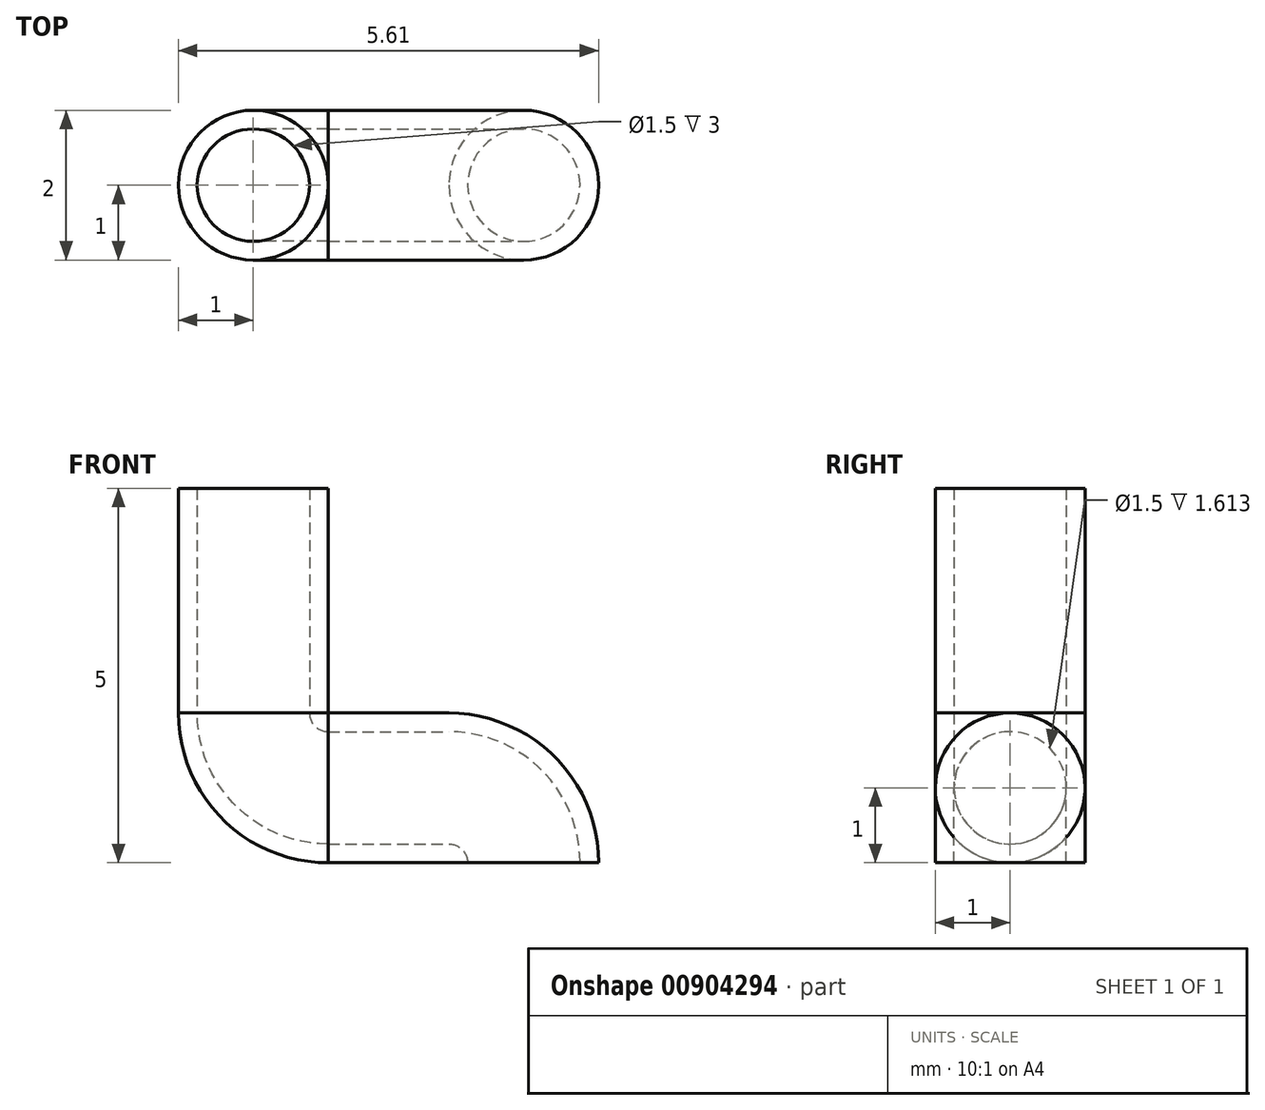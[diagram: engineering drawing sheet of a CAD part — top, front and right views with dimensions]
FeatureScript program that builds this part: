
annotation { "Feature Type Name" : "Feature", "Feature Type Description" : "" }
export const myFeature = defineFeature(function(context is Context, id is Id, definition is map)
    precondition{}
    {
        {
            var Q0;
            Q0=qCreatedBy(makeId("Top.planeOp"),FACE);
            var sketch = newSketch(context, id + "F0", { "sketchPlane" : qUnion([Q0])});
            skLineSegment(sketch, "E0.bottom", {"start": v(3.61, 0) * mm, "end": v(-3.61, 0) * mm});
            skLineSegment(sketch, "E0.top", {"start": v(3.61, 0) * mm, "end": v(-3.61, 0) * mm});
            skLineSegment(sketch, "E0.left", {"start": v(3.61, 0) * mm, "end": v(3.61, 0) * mm});
            skLineSegment(sketch, "E0.right", {"start": v(-3.61, 0) * mm, "end": v(-3.61, 0) * mm});
            skPoint(sketch, "E0.middle", {"position": v(0, 0) * mm});
            skCircle(sketch, "E1", {"center": v(-3.61, 0) * mm, "radius": 0.75 * mm});
            skCircle(sketch, "E2", {"center": v(-3.61, 0) * mm, "radius": 1 * mm});
            skCircle(sketch, "E3", {"center": v(3.61, 0) * mm, "radius": 0.75 * mm});
            skCircle(sketch, "E4", {"center": v(3.61, 0) * mm, "radius": 1 * mm});
            skSolve(sketch);
        }
        {
            var Q0;
            Q0=qCreatedBy(makeId("Front.planeOp"),FACE);
            var sketch = newSketch(context, id + "F1", { "sketchPlane" : qUnion([Q0])});
            skLineSegment(sketch, "E5.0", {"start": v(-4.61, 0) * mm, "end": v(-2.61, 0) * mm});
            skLineSegment(sketch, "E6.0", {"start": v(2.61, 0) * mm, "end": v(4.61, 0) * mm});
            skLineSegment(sketch, "E7", {"start": v(-2.61, 0) * mm, "end": v(-2.61, 2) * mm});
            skLineSegment(sketch, "E8", {"start": v(-2.61, 1) * mm, "end": v(-1.94, 1) * mm});
            skArc(sketch, "E9", {"start": v(-2.61, 1) * mm, "mid": v(-3.32, 0.7) * mm, "end": v(-3.61, 0) * mm});
            skLineSegment(sketch, "E10", {"start": v(0, 0) * mm, "end": v(0, 0.78) * mm});
            skLineSegment(sketch, "E11.MirrorCS", {"start": v(2.61, 0) * mm, "end": v(2.61, 2) * mm});
            skArc(sketch, "E12.MirrorCS", {"start": v(2.61, 1) * mm, "mid": v(3.32, 0.7) * mm, "end": v(3.61, 0) * mm});
            skSolve(sketch);
        }
        {
            var Q0;
            Q0=makeQuery(id+"F0.imprint","IMPRINT",FACE,{"disambiguationData":[TD([[makeQuery(id+"F0.imprint","IMPRINT",EDGE,{"derivedFrom":sQuery(id+"F0.wireOp",EDGE,"E1")}),-1.0]])]});
            var Q1;
            Q1=sQuery(id+"F1.wireOp",EDGE,"E9");
            sweep(context, id + "F2", {"profiles" : qUnion([Q0]), "path" : qUnion([Q1])});
        }
        {
            var Q0;
            Q0=makeQuery(id+"F0.imprint","IMPRINT",FACE,{"disambiguationData":[TD([[makeQuery(id+"F0.imprint","IMPRINT",EDGE,{"derivedFrom":sQuery(id+"F0.wireOp",EDGE,"E3")}),-1.0]])]});
            var Q1;
            Q1=sQuery(id+"F1.wireOp",EDGE,"E12.MirrorCS");
            sweep(context, id + "F3", {"profiles" : qUnion([Q0]), "path" : qUnion([Q1])});
        }
        {
            var Q0;
            Q0=makeQuery(id+"F3.opSweep","CAP_FACE",FACE,{"disambiguationData":[OSD([sQuery(id+"F0.wireOp",EDGE,"E3"),sQuery(id+"F0.wireOp",EDGE,"E4"),sQuery(id+"F1.wireOp",VERTEX,"E12.MirrorCS.start")])],"isStart":false});
            extrude(context, id + "F4", {"entities" : qUnion([Q0]), "operationType" : NewBodyOperationType.ADD, "depth" : 2.6 * mm, "offsetDistance" : 25 * mm});
        }
        {
            var Q0;
            Q0=makeQuery(id+"F2.opSweep","CAP_FACE",FACE,{"disambiguationData":[OSD([sQuery(id+"F0.wireOp",EDGE,"E1"),sQuery(id+"F0.wireOp",EDGE,"E2"),sQuery(id+"F1.wireOp",VERTEX,"E9.start")])],"isStart":false});
            extrude(context, id + "F5", {"entities" : qUnion([Q0]), "depth" : 2.6 * mm, "offsetDistance" : 25 * mm});
        }
        {
            var Q0;
            Q0=makeQuery(id+"F2.opSweep","SWEPT_BODY",BODY,{"disambiguationData":[OSD([sQuery(id+"F0.wireOp",EDGE,"E1"),sQuery(id+"F0.wireOp",EDGE,"E2"),sQuery(id+"F1.wireOp",EDGE,"E9")])]});
            var Q1;
            Q1=makeQuery(id+"F3.opSweep","SWEPT_BODY",BODY,{"disambiguationData":[OSD([sQuery(id+"F0.wireOp",EDGE,"E3"),sQuery(id+"F0.wireOp",EDGE,"E4"),sQuery(id+"F1.wireOp",EDGE,"E12.MirrorCS")])]});
            var Q2;
            Q2=makeQuery(id+"F5.opExtrude","SWEPT_BODY",BODY,{"disambiguationData":[OSD([sQuery(id+"F0.wireOp",EDGE,"E1"),sQuery(id+"F0.wireOp",EDGE,"E2"),sQuery(id+"F1.wireOp",VERTEX,"E9.start")])]});
            booleanBodies(context, id + "F6", {"operationType" : BooleanOperationType.UNION, "tools" : qUnion([Q0, Q1, Q2])});
        }
        {
            var Q0;
            Q0=qCreatedBy(makeId("Top.planeOp"),FACE);
            cPlane(context, id + "F7", {"entities" : qUnion([Q0]), "cplaneType" : CPlaneType.OFFSET, "offset" : 1 * mm, "width" : 150 * mm, "height" : 150 * mm});
        }
        {
            var Q0;
            Q0=qCreatedBy(id+"F7.planeOp",FACE);
            var sketch = newSketch(context, id + "F8", { "sketchPlane" : qUnion([Q0])});
            skCircle(sketch, "E13", {"center": v(0, 0) * mm, "radius": 1 * mm});
            skCircle(sketch, "E14", {"center": v(0, 0) * mm, "radius": 0.75 * mm});
            skSolve(sketch);
        }
        {
            var Q0;
            Q0=makeQuery(id+"F8.imprint","IMPRINT",FACE,{"disambiguationData":[TD([[makeQuery(id+"F8.imprint","IMPRINT",EDGE,{"derivedFrom":sQuery(id+"F8.wireOp",EDGE,"E13")}),1.0]])]});
            extrude(context, id + "F9", {"entities" : qUnion([Q0]), "operationType" : NewBodyOperationType.ADD, "depth" : 4 * mm, "offsetDistance" : 25 * mm});
        }
        {
            var Q0;
            Q0=makeQuery(id+"F9.opExtrude","CAP_FACE",FACE,{"disambiguationData":[OSD([sQuery(id+"F8.wireOp",EDGE,"E13"),sQuery(id+"F8.wireOp",EDGE,"E14")])],"isStart":false});
            var sketch = newSketch(context, id + "F10", { "sketchPlane" : qUnion([Q0])});
            skCircle(sketch, "E15.0", {"center": v(0, 0) * mm, "radius": 0.75 * mm});
            skSolve(sketch);
        }
        {
            var Q0;
            Q0=makeQuery(id+"F10.imprint","IMPRINT",FACE,{"disambiguationData":[TD([[makeQuery(id+"F10.imprint","IMPRINT",EDGE,{"derivedFrom":sQuery(id+"F10.wireOp",EDGE,"E15.0")}),1.0]])]});
            extrude(context, id + "F11", {"entities" : qUnion([Q0]), "operationType" : NewBodyOperationType.REMOVE, "oppositeDirection" : true, "depth" : 4 * mm, "offsetDistance" : 25 * mm});
        }
        {
            var Q0;
            Q0=qCreatedBy(makeId("Right.planeOp"),FACE);
            cPlane(context, id + "F12", {"entities" : qUnion([Q0]), "cplaneType" : CPlaneType.OFFSET, "offset" : 2 * mm, "width" : 150 * mm, "height" : 150 * mm});
        }
        {
            var Q0;
            Q0=qCreatedBy(id+"F12.planeOp",FACE);
            var sketch = newSketch(context, id + "F13", { "sketchPlane" : qUnion([Q0])});
            skCircle(sketch, "E16.0", {"center": v(0, 1) * mm, "radius": 1 * mm});
            skCircle(sketch, "E17", {"center": v(0, 1) * mm, "radius": 0.75 * mm});
            skSolve(sketch);
        }
        {
            var Q0;
            Q0=makeQuery(id+"F13.imprint","IMPRINT",FACE,{"disambiguationData":[TD([[makeQuery(id+"F13.imprint","IMPRINT",EDGE,{"derivedFrom":sQuery(id+"F13.wireOp",EDGE,"E17")}),1.0]])]});
            extrude(context, id + "F14", {"entities" : qUnion([Q0]), "operationType" : NewBodyOperationType.REMOVE, "oppositeDirection" : true, "depth" : 4 * mm, "offsetDistance" : 25 * mm});
        }
        {
            var Q0;
            Q0=qCreatedBy(makeId("Front.planeOp"),FACE);
            var sketch = newSketch(context, id + "F15", { "sketchPlane" : qUnion([Q0])});
            skLineSegment(sketch, "E18.0", {"start": v(0, 1) * mm, "end": v(1, 2) * mm});
            skLineSegment(sketch, "E19", {"start": v(2.61, 0) * mm, "end": v(-2.61, 0) * mm});
            skLineSegment(sketch, "E20.0", {"start": v(-4.61, 0) * mm, "end": v(-2.61, 0) * mm});
            skLineSegment(sketch, "E21.bottom", {"start": v(1, 2) * mm, "end": v(-4.61, 2) * mm});
            skLineSegment(sketch, "E21.top", {"start": v(1, 0) * mm, "end": v(-4.61, 0) * mm});
            skLineSegment(sketch, "E21.left", {"start": v(1, 2) * mm, "end": v(1, 0) * mm});
            skLineSegment(sketch, "E21.right", {"start": v(-4.61, 2) * mm, "end": v(-4.61, 0) * mm});
            skSolve(sketch);
        }
        {
            var Q0;
            Q0=makeQuery(id+"F15.imprint","IMPRINT",FACE,{"disambiguationData":[TD([[makeQuery(id+"F15.imprint","IMPRINT",EDGE,{"derivedFrom":sQuery(id+"F15.wireOp",EDGE,"E21.bottom")}),1.0]])]});
            extrude(context, id + "F16", {"entities" : qUnion([Q0]), "operationType" : NewBodyOperationType.REMOVE, "oppositeDirection" : true, "depth" : 25 * mm, "offsetDistance" : 25 * mm});
        }
        {
            var Q0;
            Q0=makeQuery(id+"F15.imprint","IMPRINT",FACE,{"disambiguationData":[TD([[makeQuery(id+"F15.imprint","IMPRINT",EDGE,{"derivedFrom":sQuery(id+"F15.wireOp",EDGE,"E21.bottom")}),1.0]])]});
            extrude(context, id + "F17", {"entities" : qUnion([Q0]), "operationType" : NewBodyOperationType.REMOVE, "oppositeDirection" : true, "depth" : -25 * mm, "offsetDistance" : 25 * mm});
        }
        {
            var Q0;
            Q0=qCreatedBy(makeId("Front.planeOp"),FACE);
            var sketch = newSketch(context, id + "F18", { "sketchPlane" : qUnion([Q0])});
            skLineSegment(sketch, "E22.0", {"start": v(1, 2) * mm, "end": v(1, 0) * mm});
            skLineSegment(sketch, "E23.0", {"start": v(-1, 2) * mm, "end": v(1, 2) * mm});
            skLineSegment(sketch, "E24", {"start": v(1, 1) * mm, "end": v(2.13, 1) * mm});
            skArc(sketch, "E25", {"start": v(0, 2) * mm, "mid": v(0.3, 1.3) * mm, "end": v(1, 1) * mm});
            skSolve(sketch);
        }
        {
            var Q0;
            {var subQ0=sQuery(id+"F15.wireOp",EDGE,"E21.left");Q0=makeQuery(id+"F17.boolean.opBoolean","MERGE",FACE,{"derivedFrom":[makeQuery(id+"F16.boolean.opBoolean","COPY",FACE,{"derivedFrom":makeQuery(id+"F16.opExtrude","SWEPT_FACE",FACE,{"disambiguationData":[OSD([subQ0])]})})],"fromTools":[makeQuery(id+"F17.opExtrude","SWEPT_FACE",FACE,{"disambiguationData":[OSD([subQ0])]})]});}
            var Q1;
            Q1=sQuery(id+"F18.wireOp",EDGE,"E25");
            sweep(context, id + "F19", {"profiles" : qUnion([Q0]), "path" : qUnion([Q1])});
        }
    });
